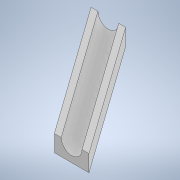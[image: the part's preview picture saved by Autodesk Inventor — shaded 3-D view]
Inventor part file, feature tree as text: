
AUTODESK INVENTOR PART (.ipt)
format: ipt  version: 2021 (Build 250183000, 183)  size: 121,856 bytes
history: native  units: mm
features: sketch x3, plane x1, loft x1
ambient origin geometry x8: Origin, YZ Plane, XZ Plane, XY Plane, X Axis, Y Axis, Z Axis, Center Point
bodies: Solid1 (feature_tree)
feature tree (5):
  sketch  "Sketch2"  dims[d1=25.0mm d2=12.0mm]
  plane  "Work Plane1"
  loft  "Loft1"
  sketch  "Sketch4"  dims[d4=5.0mm d5=7.5mm d6=54.5mm d15=5.0mm d17=25.0mm d19=5.0mm d22=7.5mm d23=0.0mm d24=90.0deg d25=0.0mm d26=90.0deg d28=12.0mm]
  sketch  "Sketch3"  dims[d3=5.0mm]
